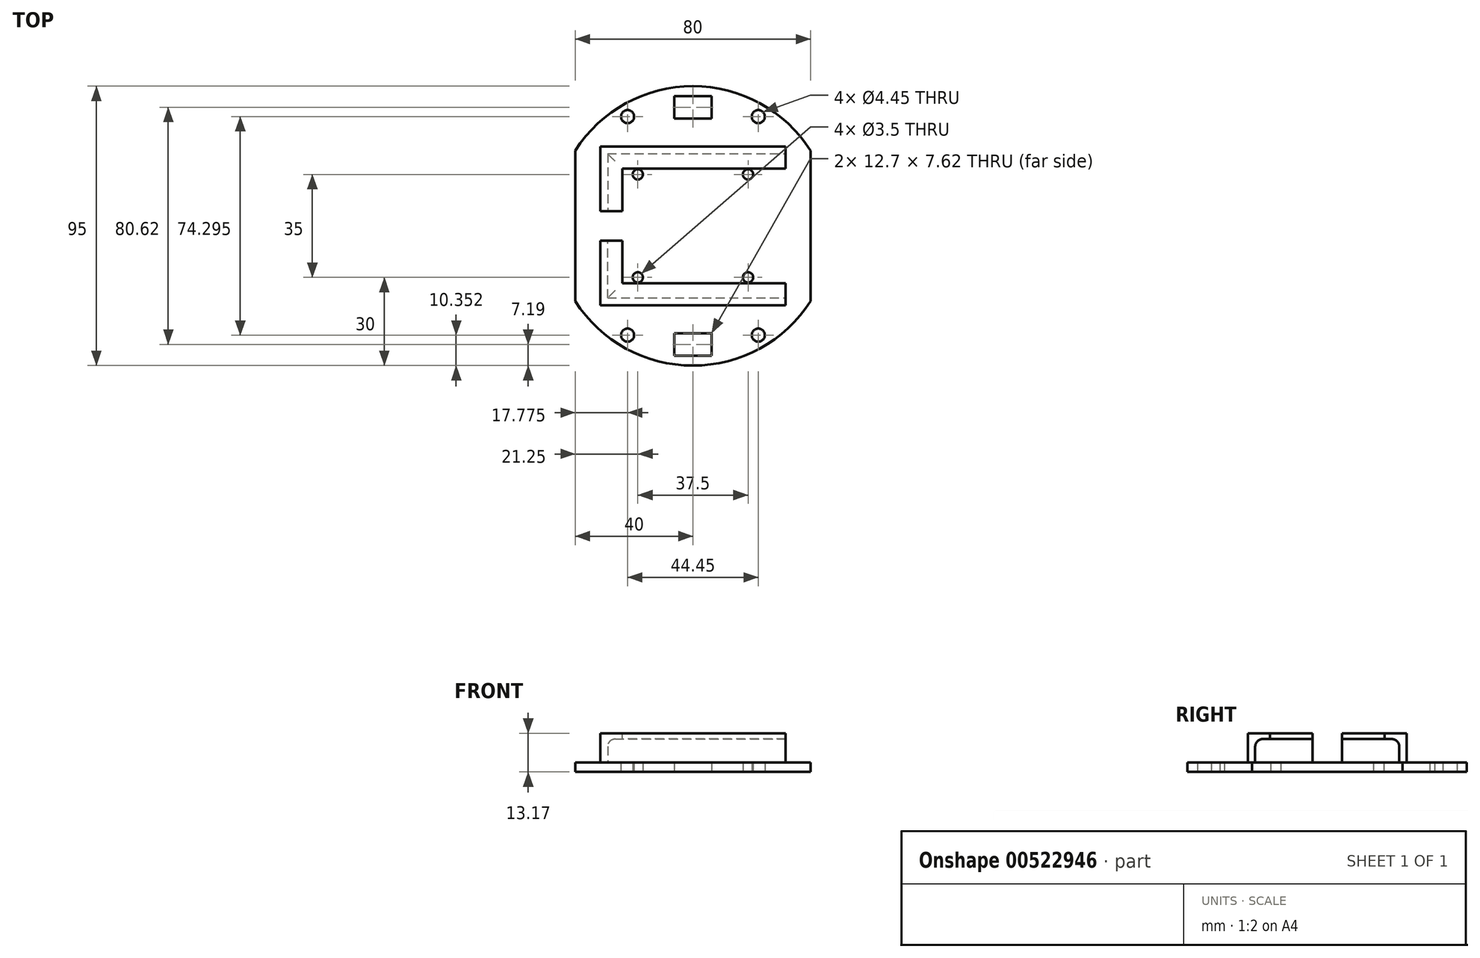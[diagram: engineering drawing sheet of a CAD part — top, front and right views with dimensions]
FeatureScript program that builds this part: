
annotation { "Feature Type Name" : "Feature", "Feature Type Description" : "" }
export const myFeature = defineFeature(function(context is Context, id is Id, definition is map)
    precondition{}
    {
        {
            var Q0;
            Q0=qCreatedBy(makeId("Top.planeOp"),FACE);
            var sketch = newSketch(context, id + "F0", { "sketchPlane" : qUnion([Q0])});
            skCircle(sketch, "E0", {"center": v(0, 0) * mm, "radius": 47.5 * mm});
            skCircle(sketch, "E1", {"center": v(22.23, -37.15) * mm, "radius": 2.22 * mm});
            skCircle(sketch, "E2.MirrorC", {"center": v(22.23, 37.15) * mm, "radius": 2.22 * mm});
            skCircle(sketch, "E3.MirrorC", {"center": v(-22.23, -37.15) * mm, "radius": 2.22 * mm});
            skCircle(sketch, "E4.MirrorC", {"center": v(-22.23, 37.15) * mm, "radius": 2.22 * mm});
            skCircle(sketch, "E5", {"center": v(18.75, -17.5) * mm, "radius": 1.75 * mm});
            skCircle(sketch, "E6", {"center": v(-18.75, -17.5) * mm, "radius": 1.75 * mm});
            skLineSegment(sketch, "E7", {"start": v(40, 25.62) * mm, "end": v(40, -25.62) * mm});
            skLineSegment(sketch, "E8.MirrorCS", {"start": v(-40, 25.62) * mm, "end": v(-40, -25.62) * mm});
            skCircle(sketch, "E9.MirrorC", {"center": v(-18.75, 17.5) * mm, "radius": 1.75 * mm});
            skCircle(sketch, "E10.MirrorC", {"center": v(18.75, 17.5) * mm, "radius": 1.75 * mm});
            skLineSegment(sketch, "E11.bottom", {"start": v(-6.35, 44.12) * mm, "end": v(6.35, 44.12) * mm});
            skLineSegment(sketch, "E11.top", {"start": v(-6.35, 36.5) * mm, "end": v(6.35, 36.5) * mm});
            skLineSegment(sketch, "E11.left", {"start": v(-6.35, 44.12) * mm, "end": v(-6.35, 36.5) * mm});
            skLineSegment(sketch, "E11.right", {"start": v(6.35, 44.12) * mm, "end": v(6.35, 36.5) * mm});
            skLineSegment(sketch, "E12.MirrorCS", {"start": v(-6.35, -44.12) * mm, "end": v(6.35, -44.12) * mm});
            skLineSegment(sketch, "E13.MirrorCS", {"start": v(-6.35, -44.12) * mm, "end": v(-6.35, -36.5) * mm});
            skLineSegment(sketch, "E14.MirrorCS", {"start": v(-6.35, -36.5) * mm, "end": v(6.35, -36.5) * mm});
            skLineSegment(sketch, "E15.MirrorCS", {"start": v(6.35, -44.12) * mm, "end": v(6.35, -36.5) * mm});
            skSolve(sketch);
        }
        {
            var Q0;
            Q0=makeQuery(id+"F0.imprint","IMPRINT",FACE,{"disambiguationData":[TD([[makeQuery(id+"F0.imprint","IMPRINT",EDGE,{"derivedFrom":sQuery(id+"F0.wireOp",EDGE,"E1")}),-1.0]])]});
            extrude(context, id + "F1", {"entities" : qUnion([Q0]), "depth" : 3.17 * mm, "offsetDistance" : 25.4 * mm});
        }
        {
            var Q0;
            Q0=makeQuery(id+"F1.opExtrude","CAP_FACE",FACE,{"disambiguationData":[OSD([sQuery(id+"F0.wireOp",EDGE,"E0"),sQuery(id+"F0.wireOp",EDGE,"E1"),sQuery(id+"F0.wireOp",EDGE,"E2.MirrorC"),sQuery(id+"F0.wireOp",EDGE,"E3.MirrorC"),sQuery(id+"F0.wireOp",EDGE,"E4.MirrorC"),sQuery(id+"F0.wireOp",EDGE,"E5"),sQuery(id+"F0.wireOp",EDGE,"E6"),sQuery(id+"F0.wireOp",EDGE,"E7"),sQuery(id+"F0.wireOp",EDGE,"E8.MirrorCS"),sQuery(id+"F0.wireOp",EDGE,"E9.MirrorC"),sQuery(id+"F0.wireOp",EDGE,"E10.MirrorC"),sQuery(id+"F0.wireOp",EDGE,"E11.bottom"),sQuery(id+"F0.wireOp",EDGE,"E11.top"),sQuery(id+"F0.wireOp",EDGE,"E11.left"),sQuery(id+"F0.wireOp",EDGE,"E11.right"),sQuery(id+"F0.wireOp",EDGE,"E12.MirrorCS"),sQuery(id+"F0.wireOp",EDGE,"E13.MirrorCS"),sQuery(id+"F0.wireOp",EDGE,"E14.MirrorCS"),sQuery(id+"F0.wireOp",EDGE,"E15.MirrorCS")])],"isStart":false});
            var sketch = newSketch(context, id + "F2", { "sketchPlane" : qUnion([Q0])});
            skLineSegment(sketch, "E16.bottom", {"start": v(-31.5, -27) * mm, "end": v(31.5, -27) * mm});
            skLineSegment(sketch, "E16.top", {"start": v(-29, -24.5) * mm, "end": v(31.5, -24.5) * mm});
            skLineSegment(sketch, "E16.left", {"start": v(-31.5, -27) * mm, "end": v(-31.5, -24.5) * mm});
            skLineSegment(sketch, "E16.right", {"start": v(31.5, -27) * mm, "end": v(31.5, -24.5) * mm});
            skLineSegment(sketch, "E17.MirrorCS", {"start": v(31.5, 27) * mm, "end": v(31.5, 24.5) * mm});
            skLineSegment(sketch, "E18.MirrorCS", {"start": v(-31.5, 27) * mm, "end": v(-31.5, 24.5) * mm});
            skLineSegment(sketch, "E19.MirrorCS", {"start": v(-29, 24.5) * mm, "end": v(31.5, 24.5) * mm});
            skLineSegment(sketch, "E20.MirrorCS", {"start": v(-31.5, 27) * mm, "end": v(31.5, 27) * mm});
            skLineSegment(sketch, "E21.left", {"start": v(-31.5, -24.5) * mm, "end": v(-31.5, -5) * mm});
            skLineSegment(sketch, "E21.right", {"start": v(-29, -24.5) * mm, "end": v(-29, -5) * mm});
            skLineSegment(sketch, "E22.MirrorCS", {"start": v(-31.5, 24.5) * mm, "end": v(-31.5, 5) * mm});
            skLineSegment(sketch, "E23.MirrorCS", {"start": v(-29, 24.5) * mm, "end": v(-29, 5) * mm});
            skLineSegment(sketch, "E24", {"start": v(-31.5, -5) * mm, "end": v(-29, -5) * mm});
            skLineSegment(sketch, "E25.MirrorCS", {"start": v(-31.5, 5) * mm, "end": v(-29, 5) * mm});
            skPoint(sketch, "E26.orphan", {"position": v(-29, 0) * mm});
            skPoint(sketch, "E27.orphan", {"position": v(-31.5, 0) * mm});
            skSolve(sketch);
        }
        {
            var Q0;
            Q0 = qSketchRegion(id + "F2", true);
            extrude(context, id + "F3", {"entities" : qUnion([Q0]), "operationType" : NewBodyOperationType.ADD, "depth" : 10 * mm, "offsetDistance" : 25.4 * mm});
        }
        {
            var Q0;
            Q0=makeQuery(id+"F3.opExtrude","CAP_FACE",FACE,{"disambiguationData":[OSD([sQuery(id+"F2.wireOp",EDGE,"E16.bottom"),sQuery(id+"F2.wireOp",EDGE,"E16.top"),sQuery(id+"F2.wireOp",EDGE,"E16.left"),sQuery(id+"F2.wireOp",EDGE,"E16.right"),sQuery(id+"F2.wireOp",EDGE,"E21.left"),sQuery(id+"F2.wireOp",EDGE,"E21.right"),sQuery(id+"F2.wireOp",EDGE,"E24")])],"isStart":false});
            var sketch = newSketch(context, id + "F4", { "sketchPlane" : qUnion([Q0])});
            skLineSegment(sketch, "E28.bottom", {"start": v(31.5, -27) * mm, "end": v(-31.5, -27) * mm});
            skLineSegment(sketch, "E28.top", {"start": v(31.5, -19.5) * mm, "end": v(-24, -19.5) * mm});
            skLineSegment(sketch, "E28.left", {"start": v(31.5, -27) * mm, "end": v(31.5, -19.5) * mm});
            skLineSegment(sketch, "E28.right", {"start": v(-31.5, -27) * mm, "end": v(-31.5, -19.5) * mm});
            skLineSegment(sketch, "E29.bottom", {"start": v(-31.5, -5) * mm, "end": v(-24, -5) * mm});
            skLineSegment(sketch, "E29.left", {"start": v(-31.5, -5) * mm, "end": v(-31.5, -19.5) * mm});
            skLineSegment(sketch, "E29.right", {"start": v(-24, -5) * mm, "end": v(-24, -19.5) * mm});
            skLineSegment(sketch, "E30.MirrorCS", {"start": v(-31.5, 5) * mm, "end": v(-24, 5) * mm});
            skLineSegment(sketch, "E31.MirrorCS", {"start": v(-31.5, 27) * mm, "end": v(-31.5, 19.5) * mm});
            skLineSegment(sketch, "E32.MirrorCS", {"start": v(31.5, 27) * mm, "end": v(31.5, 19.5) * mm});
            skLineSegment(sketch, "E33.MirrorCS", {"start": v(-24, 5) * mm, "end": v(-24, 19.5) * mm});
            skLineSegment(sketch, "E34.MirrorCS", {"start": v(-31.5, 5) * mm, "end": v(-31.5, 14.29) * mm});
            skLineSegment(sketch, "E35.MirrorCS", {"start": v(31.5, 19.5) * mm, "end": v(-24, 19.5) * mm});
            skLineSegment(sketch, "E36.MirrorCS", {"start": v(31.5, 27) * mm, "end": v(-31.5, 27) * mm});
            skPoint(sketch, "E37.orphan", {"position": v(-31.5, -18.86) * mm});
            skPoint(sketch, "E38.orphan", {"position": v(-31.5, 18.86) * mm});
            skLineSegment(sketch, "E39", {"start": v(-31.5, 14.29) * mm, "end": v(-31.5, 20.74) * mm});
            skSolve(sketch);
        }
        {
            var Q0;
            Q0 = qSketchRegion(id + "F4", true);
            extrude(context, id + "F5", {"entities" : qUnion([Q0]), "operationType" : NewBodyOperationType.ADD, "oppositeDirection" : true, "depth" : 2 * mm, "offsetDistance" : 25.4 * mm});
        }
        {
            var Q0;
            Q0=makeQuery(id+"F5.boolean.opBoolean","INTERSECT",EDGE,{"derivedFrom":[makeQuery(id+"F3.opExtrude","SWEPT_FACE",FACE,{"disambiguationData":[OSD([sQuery(id+"F2.wireOp",EDGE,"E16.top")])]}),makeQuery(id+"F5.opExtrude","CAP_FACE",FACE,{"disambiguationData":[OSD([sQuery(id+"F4.wireOp",EDGE,"E28.bottom"),sQuery(id+"F4.wireOp",EDGE,"E28.top"),sQuery(id+"F4.wireOp",EDGE,"E28.left"),sQuery(id+"F4.wireOp",EDGE,"E28.right"),sQuery(id+"F4.wireOp",EDGE,"E29.bottom"),sQuery(id+"F4.wireOp",EDGE,"E29.left"),sQuery(id+"F4.wireOp",EDGE,"E29.right")])],"isStart":false})]});
            var Q1;
            Q1=makeQuery(id+"F5.boolean.opBoolean","INTERSECT",EDGE,{"derivedFrom":[makeQuery(id+"F3.opExtrude","SWEPT_FACE",FACE,{"disambiguationData":[OSD([sQuery(id+"F2.wireOp",EDGE,"E19.MirrorCS")])]}),makeQuery(id+"F5.opExtrude","CAP_FACE",FACE,{"disambiguationData":[OSD([sQuery(id+"F4.wireOp",EDGE,"E30.MirrorCS"),sQuery(id+"F4.wireOp",EDGE,"E31.MirrorCS"),sQuery(id+"F4.wireOp",EDGE,"E32.MirrorCS"),sQuery(id+"F4.wireOp",EDGE,"E33.MirrorCS"),sQuery(id+"F4.wireOp",EDGE,"E34.MirrorCS"),sQuery(id+"F4.wireOp",EDGE,"E35.MirrorCS"),sQuery(id+"F4.wireOp",EDGE,"E36.MirrorCS"),sQuery(id+"F4.wireOp",EDGE,"E39")])],"isStart":false})]});
            var Q2;
            Q2=makeQuery(id+"F5.boolean.opBoolean","INTERSECT",EDGE,{"derivedFrom":[makeQuery(id+"F3.opExtrude","SWEPT_FACE",FACE,{"disambiguationData":[OSD([sQuery(id+"F2.wireOp",EDGE,"E21.right")])]}),makeQuery(id+"F5.opExtrude","CAP_FACE",FACE,{"disambiguationData":[OSD([sQuery(id+"F4.wireOp",EDGE,"E28.bottom"),sQuery(id+"F4.wireOp",EDGE,"E28.top"),sQuery(id+"F4.wireOp",EDGE,"E28.left"),sQuery(id+"F4.wireOp",EDGE,"E28.right"),sQuery(id+"F4.wireOp",EDGE,"E29.bottom"),sQuery(id+"F4.wireOp",EDGE,"E29.left"),sQuery(id+"F4.wireOp",EDGE,"E29.right")])],"isStart":false})]});
            var Q3;
            Q3=makeQuery(id+"F5.boolean.opBoolean","INTERSECT",EDGE,{"derivedFrom":[makeQuery(id+"F3.opExtrude","SWEPT_FACE",FACE,{"disambiguationData":[OSD([sQuery(id+"F2.wireOp",EDGE,"E23.MirrorCS")])]}),makeQuery(id+"F5.opExtrude","CAP_FACE",FACE,{"disambiguationData":[OSD([sQuery(id+"F4.wireOp",EDGE,"E30.MirrorCS"),sQuery(id+"F4.wireOp",EDGE,"E31.MirrorCS"),sQuery(id+"F4.wireOp",EDGE,"E32.MirrorCS"),sQuery(id+"F4.wireOp",EDGE,"E33.MirrorCS"),sQuery(id+"F4.wireOp",EDGE,"E34.MirrorCS"),sQuery(id+"F4.wireOp",EDGE,"E35.MirrorCS"),sQuery(id+"F4.wireOp",EDGE,"E36.MirrorCS"),sQuery(id+"F4.wireOp",EDGE,"E39")])],"isStart":false})]});
            fillet(context, id + "F6", {"entities" : qUnion([Q0, Q1, Q2, Q3]), "radius" : 2.54 * mm, "tangentPropagation" : true, "allowEdgeOverflow" : false});
        }
    });
